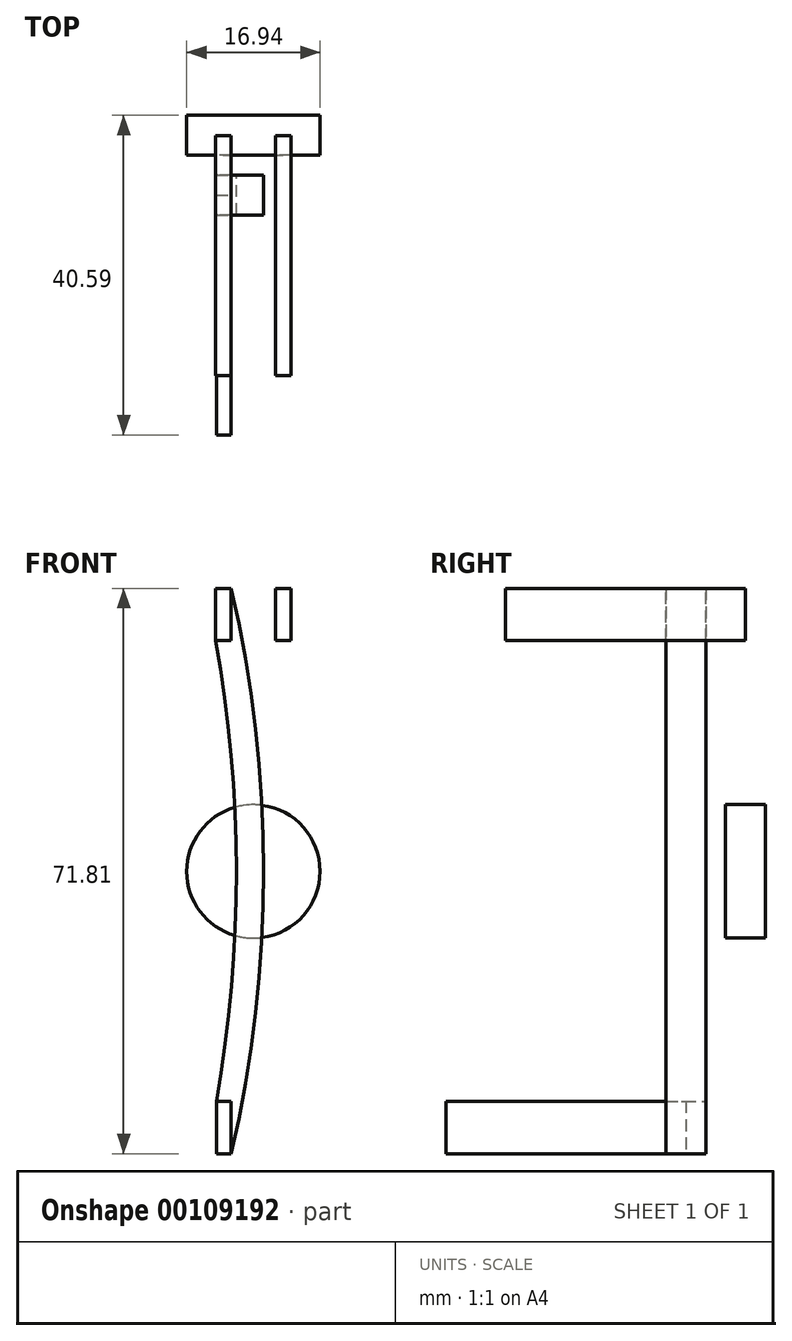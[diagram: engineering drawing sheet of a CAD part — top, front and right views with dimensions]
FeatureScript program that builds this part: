
annotation { "Feature Type Name" : "Feature", "Feature Type Description" : "" }
export const myFeature = defineFeature(function(context is Context, id is Id, definition is map)
    precondition{}
    {
        {
            var Q0;
            Q0=qCreatedBy(makeId("Front.planeOp"),FACE);
            var sketch = newSketch(context, id + "F0", { "sketchPlane" : qUnion([Q0])});
            skArc(sketch, "E0", {"start": v(-4.69, -29.2) * mm, "mid": v(-2.16, 0.08) * mm, "end": v(-4.81, 29.34) * mm});
            skLineSegment(sketch, "E1", {"start": v(0, 50.65) * mm, "end": v(0, -48.53) * mm, "construction": true});
            skLineSegment(sketch, "E2.bottom", {"start": v(-4.81, 29.34) * mm, "end": v(-2.81, 29.34) * mm});
            skLineSegment(sketch, "E2.top", {"start": v(-4.81, 35.95) * mm, "end": v(-2.81, 35.95) * mm});
            skLineSegment(sketch, "E2.left", {"start": v(-4.81, 29.34) * mm, "end": v(-4.81, 35.95) * mm});
            skLineSegment(sketch, "E2.right", {"start": v(-2.81, 29.34) * mm, "end": v(-2.81, 35.95) * mm});
            skLineSegment(sketch, "E3.bottom", {"start": v(-4.69, -29.2) * mm, "end": v(-2.81, -29.2) * mm});
            skLineSegment(sketch, "E3.top", {"start": v(-4.69, -35.86) * mm, "end": v(-2.81, -35.86) * mm});
            skLineSegment(sketch, "E3.left", {"start": v(-4.69, -29.2) * mm, "end": v(-4.69, -35.86) * mm});
            skLineSegment(sketch, "E3.right", {"start": v(-2.81, -29.2) * mm, "end": v(-2.81, -35.86) * mm});
            skArc(sketch, "E4", {"start": v(-2.81, -35.86) * mm, "mid": v(1.3, 0.04) * mm, "end": v(-2.81, 35.95) * mm});
            skSolve(sketch);
        }
        {
            var Q0;
            Q0=makeQuery(id+"F0.imprint","IMPRINT",FACE,{"disambiguationData":[TD([[makeQuery(id+"F0.imprint","IMPRINT",EDGE,{"derivedFrom":sQuery(id+"F0.wireOp",EDGE,"E0")}),-1.0]])]});
            var Q1;
            Q1=makeQuery(id+"F0.imprint","IMPRINT",FACE,{"disambiguationData":[TD([[makeQuery(id+"F0.imprint","IMPRINT",EDGE,{"derivedFrom":sQuery(id+"F0.wireOp",EDGE,"E2.bottom")}),1.0]])]});
            var Q2;
            Q2=makeQuery(id+"F0.imprint","IMPRINT",FACE,{"disambiguationData":[TD([[makeQuery(id+"F0.imprint","IMPRINT",EDGE,{"derivedFrom":sQuery(id+"F0.wireOp",EDGE,"E3.bottom")}),-1.0]])]});
            extrude(context, id + "F1", {"entities" : qUnion([Q0, Q1, Q2]), "endBound" : BoundingType.SYMMETRIC, "depth" : 5.08 * mm});
        }
        {
            var Q0;
            Q0=makeQuery(id+"F0.imprint","IMPRINT",FACE,{"disambiguationData":[TD([[makeQuery(id+"F0.imprint","IMPRINT",EDGE,{"derivedFrom":sQuery(id+"F0.wireOp",EDGE,"E3.bottom")}),-1.0]])]});
            var Q1;
            Q1=makeQuery(id+"F0.imprint","IMPRINT",FACE,{"disambiguationData":[TD([[makeQuery(id+"F0.imprint","IMPRINT",EDGE,{"derivedFrom":sQuery(id+"F0.wireOp",EDGE,"E2.bottom")}),1.0]])]});
            extrude(context, id + "F2", {"entities" : qUnion([Q0, Q1]), "depth" : 30.48 * mm});
        }
        {
            var Q0;
            Q0=makeQuery(id+"F2.opExtrude","SWEPT_BODY",BODY,{"disambiguationData":[OSD([sQuery(id+"F0.wireOp",EDGE,"E2.bottom"),sQuery(id+"F0.wireOp",EDGE,"E2.top"),sQuery(id+"F0.wireOp",EDGE,"E2.left"),sQuery(id+"F0.wireOp",EDGE,"E2.right")])]});
            transform(context, id + "F3", {"entities" : qUnion([Q0]), "transformType" : TransformType.TRANSLATION_3D, "dx" : 0 * mm, "dy" : 7.56 * mm, "dz" : 0 * mm, "makeCopy" : false});
        }
        {
            var Q0;
            Q0=makeQuery(id+"F2.opExtrude","SWEPT_BODY",BODY,{"disambiguationData":[OSD([sQuery(id+"F0.wireOp",EDGE,"E2.bottom"),sQuery(id+"F0.wireOp",EDGE,"E2.top"),sQuery(id+"F0.wireOp",EDGE,"E2.left"),sQuery(id+"F0.wireOp",EDGE,"E2.right")])]});
            var Q1;
            Q1=qCreatedBy(makeId("Right.planeOp"),FACE);
            mirror(context, id + "F4", {"operationType" : NewBodyOperationType.ADD, "entities" : qUnion([Q0]), "mirrorPlane" : qUnion([Q1])});
        }
        {
            var Q0;
            Q0=qCreatedBy(makeId("Front.planeOp"),FACE);
            var sketch = newSketch(context, id + "F5", { "sketchPlane" : qUnion([Q0])});
            skCircle(sketch, "E5", {"center": v(0, 0) * mm, "radius": 8.47 * mm});
            skSolve(sketch);
        }
        {
            var Q0;
            Q0=qSketchRegion(id+"F5",true);
            extrude(context, id + "F6", {"entities" : qUnion([Q0]), "oppositeDirection" : true, "depth" : 5.08 * mm});
        }
        {
            var Q0;
            Q0=makeQuery(id+"F6.opExtrude","SWEPT_BODY",BODY,{"disambiguationData":[OSD([sQuery(id+"F5.wireOp",EDGE,"E5")])]});
            transform(context, id + "F7", {"entities" : qUnion([Q0]), "transformType" : TransformType.TRANSLATION_3D, "dx" : 0 * mm, "dy" : 5.03 * mm, "dz" : 0 * mm, "makeCopy" : false});
        }
    });
